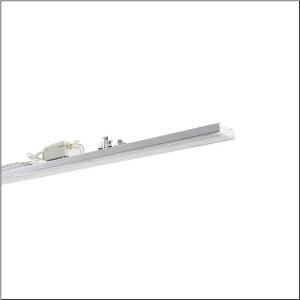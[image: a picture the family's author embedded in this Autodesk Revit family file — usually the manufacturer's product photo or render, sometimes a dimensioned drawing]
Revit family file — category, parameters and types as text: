
# Revit family: licross_21_recessed_mo_52tl10de45xg
name_source: partatom
category: Lighting Fixtures
units: mm (PartAtom-declared; Revit-internal decimal feet)

## family parameters
Cut with Voids When Loaded = No
Host = Face
Light Source = No
Part Type = Normal
Room Calculation Point = No
Round Connector Dimension = Use Diameter
Shared = No

## types (1)
- --- (1 x LED, 5000 lm, 29.9 W, 4000K)
    Apparent Load = 30 VA
    CIE Flux Codes = 50 81 96 100 100
    Color Rendering = 80
    Color Temperature = 4000K
    Default Elevation = 1800 mm
    Description = Licross 21 Recessed MO, luminaire insert, of sheet steel, galvanised, coil coated, white, length: 750mm, width: 66mm, height: 67mm, LED rated luminous flux: 5.000lm, light colour: 840, SDCM (Standard Deviation of Colour Matching)MacAdam ≤ 3 SDCM (initial), control gear: DALI 2, with plug, 5-pole, with phase selection, mains connection: 220..240V, AC, 50/60Hz, rated input power: 30W, internal wiring halogen-free, primary optical cover: cover, of PMMA, light emission: direct distribution, primary light characteristic: symmetric, protection rating (complete): IP40, insulation class (complete): insulation class I (protective earthing), certification: CE, ENEC, VDE, UKCA, protection symbol: D if used in an environment without relevant dust loads with corresponding accessories, impact resistance: IK06, permissible ambient temperature for indoor applications: -25..+35°C, corresponds to IFS (International Featured Standards) requirements for safety and quality in the food industry, reducing of maximum allowable ambient temperature of 5°C with ceiling mounting, LABS conformity tested according to VDMA 24364:2018-05, The light source and the operating device comply with the requirements of the Ecodesign Regulation (EU) 2019/2020 and are replaceable in accordance with this regulation, packaging unit: 1 piece
    Height = 58 mm
    Lamp = 1 x LED
    Lamp Light Flux = 5000 lm
    Lamp Power = 29.9 W
    Lamp count = 1
    Length = 750 mm
    Luminous efficacy = 167 lm/W
    Manufacturer = Siteco
    ModVariant = No
    Model = 52TL10DE45XG
    Mounting Place = Ceiling
    Mounting Type = Pendant
    Number of Poles = 1
    OnlyDefault = Yes
    Power Factor = 1
    Product Name = Licross 21 Recessed MO
    Product group = luminaire insert | ceiling pendant
    ProductGroupID = 901
    Protection Class = Protection class I
    Protection Degree = IP 40
    RLX_Detail_Level = 1
    RLX_Emergency_Light_Flux = 0 lm
    RLX_Emergency_Type = 0
    RLX_Emergency_Type_DB = No
    RlxData = <blob elided: 28961 chars, md5=a38657e6>
    Socket = socket
    Standby Power = 0 W
    System Light Flux = 5000 lm
    System Power = 30 W
    Type Comments = factory setting: luminous flux: 100 % | dim-lin: 254 | 390 mA
    Type Image = l_1296930.jpg
    URL = http://relux.com
    VarID = @adj_129399
    Voltage = 0 V
    Weight = 0.00 kg
    Width = 66 mm

## geometry (parser evidence)
native form markers: Blend x4, Sweep x8
no freeform markers — native parametric forms only
